# Revit family: Zumtobel ONDARIA 2
name_source: partatom
category: Leuchten
revit_build: Autodesk Revit 2016 (Build: 20150714_1515(x64)
units: mm (PartAtom-declared; Revit-internal decimal feet)

## family parameters
Basisbauteil = Fläche
Beim Laden mit Abzugskörper schneiden = Nein
Bemaßung runder Anschluss = Durchmesser verwenden
Gemeinsam genutzt = Nein
Lichtquelle = Ja
OmniClass-Nummer = 23.80.70.11
OmniClass-Titel = Luminaries for Internal Lighting
Raumberechnungspunkt = Nein
Teiletyp = Normal

## types (4) — shared parameters
Baugruppenkennzeichen = D5020200
Beschreibung = Circular LED luminaire
Emissionsform beim Rendern sichtbar = Ja
Farbfilter = 16777215
Farbtemperaturverschiebung bei Dämpfen der Lampe = <Keine Auswahl>
Height = 84.5 mm  [stored 0.277231 ft]
Hersteller = Zumtobel Lighting
Lampe = LED
Neigungswinkel = 90.00°
URL = http://www.zumtobel.com
Voltage = 230 V
zero-valued in all types: Vorgabe-Ansicht

## per-type parameters (varying)
| type | Back Distance A | Back Distance B | Back Distance Offset B | Back Radius | Datei für fotometrisches Netz | Length | Modell | Radius | Scheinlast | Von Kreisdurchmesser aussenden | Width |
| ONDARIA 2 D1150 LED | 398.4 mm  [stored 1.30709 ft] | 345 mm  [stored 1.13189 ft] | 115 mm  [stored 0.377297 ft] | 260 mm  [stored 0.853018 ft] | D35145AA_ONDA2_D870_LED7000-840.IES | 1150 mm | 42183392 | 575 mm | 65 VA | 1090.3 mm | 1150 mm |
| ONDARIA 2 D590 LED | 311.8 mm  [stored 1.02297 ft] | 270 mm  [stored 0.885827 ft] | 90 mm | 210 mm  [stored 0.688976 ft] | D35145AA_ONDA2_D590_LED2900-840.IES | 590 mm  [stored 1.9357 ft] | 42183391 | 295 mm  [stored 0.967848 ft] | 28 VA | 530.3 mm  [stored 1.73983 ft] | 590 mm  [stored 1.9357 ft] |
| ONDARIA 2 D870 LED | 210 mm  [stored 0.688976 ft] | 180 mm  [stored 0.590551 ft] | 90 mm | 160 mm  [stored 0.524934 ft] | D35145AA_ONDA2_D870_LED7000-840.IES | 400 mm  [stored 1.31234 ft] | 42183392 | 200 mm  [stored 0.656168 ft] | 65 VA | 340.3 mm  [stored 1.11647 ft] | 400 mm  [stored 1.31234 ft] |
| ONDARIA 2 D400 LED | 311.8 mm  [stored 1.02297 ft] | 270 mm  [stored 0.885827 ft] | 90 mm | 210 mm  [stored 0.688976 ft] | 42186627_(STD_LEO).IES | 400 mm  [stored 1.31234 ft] | 42186627 | 200 mm  [stored 0.656168 ft] | 20 VA | 340.3 mm  [stored 1.11647 ft] | 400 mm  [stored 1.31234 ft] |

note: [stored X ft] marks values corroborated as IEEE doubles in the binary element streams (Revit-internal decimal feet)

## geometry (parser evidence)
native form markers: Blend x2, Sweep x3
no freeform markers — native parametric forms only
